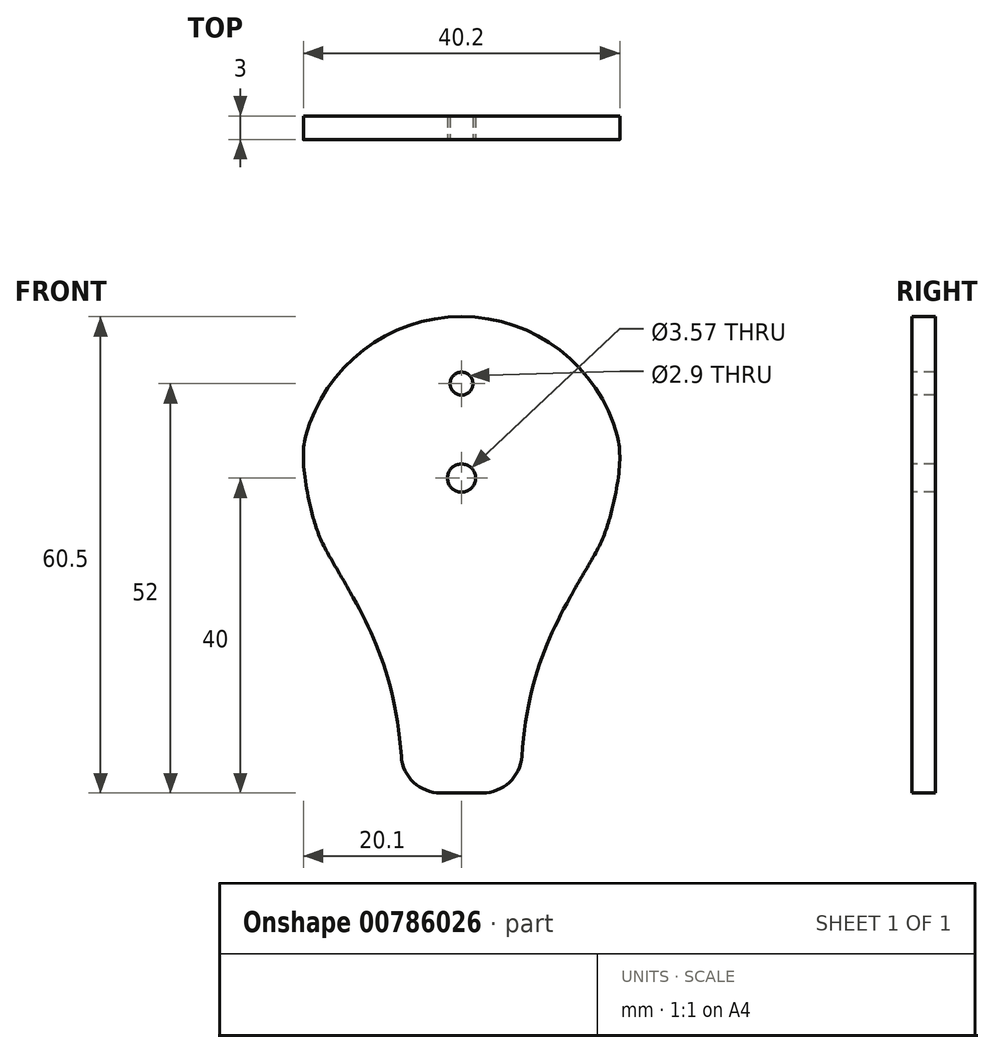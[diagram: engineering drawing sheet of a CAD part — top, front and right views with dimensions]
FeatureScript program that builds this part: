
annotation { "Feature Type Name" : "Feature", "Feature Type Description" : "" }
export const myFeature = defineFeature(function(context is Context, id is Id, definition is map)
    precondition{}
    {
        {
            var Q0;
            Q0=qCreatedBy(makeId("Front.planeOp"),FACE);
            var sketch = newSketch(context, id + "F0", { "sketchPlane" : qUnion([Q0])});
            skLineSegment(sketch, "E0.bottom", {"start": v(7.5, 0) * mm, "end": v(-7.5, 0) * mm, "construction": true});
            skLineSegment(sketch, "E0.top", {"start": v(7.5, -40) * mm, "end": v(-7.5, -40) * mm});
            skLineSegment(sketch, "E0.left", {"start": v(7.5, 0) * mm, "end": v(7.5, -40) * mm, "construction": true});
            skLineSegment(sketch, "E0.right", {"start": v(-7.5, 0) * mm, "end": v(-7.5, -40) * mm, "construction": true});
            skPoint(sketch, "E0.middle", {"position": v(0, -20) * mm});
            skCircle(sketch, "E1", {"center": v(0, 0) * mm, "radius": 19.5 * mm});
            skCircle(sketch, "E2", {"center": v(0, 0) * mm, "radius": 20.5 * mm});
            skLineSegment(sketch, "E3", {"start": v(0, 0) * mm, "end": v(19.8, 5.3) * mm, "construction": true});
            skLineSegment(sketch, "E4", {"start": v(0, 0) * mm, "end": v(18.84, -5.05) * mm, "construction": true});
            skLineSegment(sketch, "E5", {"start": v(0, 0) * mm, "end": v(16.89, -9.75) * mm, "construction": true});
            skLineSegment(sketch, "E6", {"start": v(0, 0) * mm, "end": v(17.75, 10.25) * mm, "construction": true});
            skLineSegment(sketch, "E7", {"start": v(19.8, 5.3) * mm, "end": v(19.8, 5.3) * mm});
            skLineSegment(sketch, "E8", {"start": v(16.89, -9.75) * mm, "end": v(11.89, -18.41) * mm});
            skLineSegment(sketch, "E9", {"start": v(0, -40) * mm, "end": v(0, 20.5) * mm, "construction": true});
            skFitSpline(sketch, "E10.MirrorCS", {"points": [v(-16.89, -9.75) * mm, v(-7.5, -40) * mm], "startDerivative": vector(15, -25.98) * mm, "endDerivative": vector(0, -45) * mm});
            skLineSegment(sketch, "E11.MirrorCS", {"start": v(0, 0) * mm, "end": v(-17.75, 10.25) * mm});
            skFitSpline(sketch, "E12", {"points": [v(19.8, 5.3) * mm, v(18.84, -5.05) * mm], "startDerivative": vector(1.96, -7.3) * mm, "endDerivative": vector(-3.42, -12.77) * mm});
            skLineSegment(sketch, "E13", {"start": v(19.8, 5.3) * mm, "end": v(20.45, 2.87) * mm, "construction": true});
            skLineSegment(sketch, "E14", {"start": v(18.84, -5.05) * mm, "end": v(19.98, -0.79) * mm, "construction": true});
            skLineSegment(sketch, "E15.MirrorCS", {"start": v(0, 0) * mm, "end": v(-17.75, 10.25) * mm, "construction": true});
            skLineSegment(sketch, "E16.MirrorCS", {"start": v(0, 0) * mm, "end": v(-19.8, 5.3) * mm, "construction": true});
            skLineSegment(sketch, "E17.MirrorCS", {"start": v(0, 0) * mm, "end": v(-18.84, -5.05) * mm, "construction": true});
            skLineSegment(sketch, "E18.MirrorCS", {"start": v(0, 0) * mm, "end": v(-16.89, -9.75) * mm, "construction": true});
            skFitSpline(sketch, "E19.MirrorCS", {"points": [v(-19.8, 5.3) * mm, v(-18.84, -5.05) * mm], "startDerivative": vector(-1.96, -7.3) * mm, "endDerivative": vector(3.42, -12.77) * mm});
            skFitSpline(sketch, "E20.MirrorCS", {"points": [v(16.89, -9.75) * mm, v(7.5, -40) * mm], "startDerivative": vector(-15, -25.98) * mm, "endDerivative": vector(0, -45) * mm});
            skLineSegment(sketch, "E21.bottom", {"start": v(-7.5, -40) * mm, "end": v(7.5, -40) * mm});
            skLineSegment(sketch, "E21.top", {"start": v(-7.5, -296) * mm, "end": v(7.5, -296) * mm});
            skLineSegment(sketch, "E21.left", {"start": v(-7.5, -40) * mm, "end": v(-7.5, -296) * mm});
            skLineSegment(sketch, "E21.right", {"start": v(7.5, -40) * mm, "end": v(7.5, -296) * mm});
            skLineSegment(sketch, "E22.bottom", {"start": v(2.87, -299) * mm, "end": v(-2.87, -299) * mm});
            skLineSegment(sketch, "E22.top", {"start": v(2.87, -293) * mm, "end": v(-2.87, -293) * mm});
            skLineSegment(sketch, "E22.left", {"start": v(2.87, -299) * mm, "end": v(2.87, -293) * mm});
            skLineSegment(sketch, "E22.right", {"start": v(-2.87, -299) * mm, "end": v(-2.87, -293) * mm});
            skPoint(sketch, "E22.middle", {"position": v(0, -296) * mm});
            skSolve(sketch);
        }
        {
            var Q0;
            {var subQ0=sQuery(id+"F0.wireOp",EDGE,"E19.MirrorCS");Q0=makeQuery(id+"F0.imprint","IMPRINT",FACE,{"disambiguationData":[TD([[makeQuery(id+"F0.imprint","IMPRINT",EDGE,{"derivedFrom":subQ0}),1.0]])]});}
            var Q1;
            {var subQ0=sQuery(id+"F0.wireOp",EDGE,"E12");Q1=makeQuery(id+"F0.imprint","IMPRINT",FACE,{"disambiguationData":[TD([[makeQuery(id+"F0.imprint","IMPRINT",EDGE,{"derivedFrom":subQ0}),-1.0]])]});}
            var Q2;
            {var subQ0=sQuery(id+"F0.wireOp",EDGE,"E1");var subQ4=makeQuery(id+"F0.imprint","INTERSECT",VERTEX,{"derivedFrom":[subQ0,sQuery(id+"F0.wireOp",EDGE,"E19.MirrorCS")]});Q2=makeQuery(id+"F0.imprint","IMPRINT",FACE,{"disambiguationData":[TD([[makeQuery(id+"F0.imprint","IMPRINT",EDGE,{"disambiguationData":[TD([[subQ4,1.0]])],"derivedFrom":subQ0}),1.0]])]});}
            var Q3;
            {var subQ3=sQuery(id+"F0.wireOp",EDGE,"E10.MirrorCS");var subQ5=sQuery(id+"F0.wireOp",EDGE,"E2");var subQ6=makeQuery(id+"F0.imprint","INTERSECT",VERTEX,{"derivedFrom":[subQ5,subQ3]});Q3=makeQuery(id+"F0.imprint","IMPRINT",FACE,{"disambiguationData":[TD([[makeQuery(id+"F0.imprint","IMPRINT",EDGE,{"disambiguationData":[TD([[subQ6,-1.0]])],"derivedFrom":subQ5}),1.0]])]});}
            var Q4;
            {var subQ1=sQuery(id+"F0.wireOp",EDGE,"E0.top");Q4=makeQuery(id+"F0.imprint","IMPRINT",FACE,{"disambiguationData":[TD([[makeQuery(id+"F0.imprint","IMPRINT",EDGE,{"derivedFrom":subQ1}),-1.0]])]});}
            var Q5;
            {var subQ0=sQuery(id+"F0.wireOp",EDGE,"E8");var subQ1=sQuery(id+"F0.wireOp",EDGE,"E2");var subQ2=makeQuery(id+"F0.imprint","INTERSECT",VERTEX,{"derivedFrom":[subQ1,subQ0]});Q5=makeQuery(id+"F0.imprint","IMPRINT",FACE,{"disambiguationData":[TD([[makeQuery(id+"F0.imprint","IMPRINT",EDGE,{"disambiguationData":[TD([[subQ2,-1.0]])],"derivedFrom":subQ1}),1.0]])]});}
            var Q6;
            {var subQ0=sQuery(id+"F0.wireOp",EDGE,"E21.bottom");Q6=makeQuery(id+"F0.imprint","IMPRINT",FACE,{"disambiguationData":[TD([[makeQuery(id+"F0.imprint","IMPRINT",EDGE,{"derivedFrom":subQ0}),1.0]])]});}
            var Q7;
            Q7=makeQuery(id+"F0.imprint","IMPRINT",FACE,{"disambiguationData":[TD([[makeQuery(id+"F0.imprint","IMPRINT",EDGE,{"derivedFrom":sQuery(id+"F0.wireOp",EDGE,"E21.bottom")}),-1.0]])]});
            extrude(context, id + "F1", {"entities" : qUnion([Q0, Q1, Q2, Q3, Q4, Q5, Q6, Q7]), "depth" : 3 * mm, "offsetDistance" : 25 * mm});
        }
        {
            var Q0;
            Q0=makeQuery(id+"F1.opExtrude","CAP_FACE",FACE,{"disambiguationData":[OSD([sQuery(id+"F0.wireOp",EDGE,"E0.top"),sQuery(id+"F0.wireOp",EDGE,"E1"),sQuery(id+"F0.wireOp",EDGE,"E2"),sQuery(id+"F0.wireOp",EDGE,"7a9026b3-197f-48e2-9b81-13cee80a4807"),sQuery(id+"F0.wireOp",EDGE,"0a668d27-42bc-4e6d-9f5e-2706f69a0711"),sQuery(id+"F0.wireOp",EDGE,"f3387c69-d86e-4529-9347-0b486354b344.MirrorCS"),sQuery(id+"F0.wireOp",EDGE,"E10.MirrorCS")])],"isStart":false});
            var sketch = newSketch(context, id + "F2", { "sketchPlane" : qUnion([Q0])});
            skCircle(sketch, "E23", {"center": v(0, 0) * mm, "radius": 1.79 * mm});
            skSolve(sketch);
        }
        {
            var Q0;
            Q0=qSketchRegion(id+"F2",true);
            extrude(context, id + "F3", {"entities" : qUnion([Q0]), "operationType" : NewBodyOperationType.REMOVE, "oppositeDirection" : true, "depth" : 25 * mm, "offsetDistance" : 25 * mm});
        }
        {
            var Q0;
            Q0=makeQuery(id+"F1.opExtrude","SWEPT_EDGE",EDGE,{"disambiguationData":[OSD([sQuery(id+"F0.wireOp",EDGE,"E21.top"),sQuery(id+"F0.wireOp",EDGE,"E21.left")])]});
            var Q1;
            Q1=makeQuery(id+"F1.opExtrude","SWEPT_EDGE",EDGE,{"disambiguationData":[OSD([sQuery(id+"F0.wireOp",EDGE,"E21.top"),sQuery(id+"F0.wireOp",EDGE,"E21.right")])]});
            fillet(context, id + "F4", {"entities" : qUnion([Q0, Q1]), "radius" : 5 * mm, "tangentPropagation" : true, "allowEdgeOverflow" : false});
        }
        {
            var Q0;
            Q0=makeQuery(id+"F1.opExtrude","CAP_FACE",FACE,{"disambiguationData":[OSD([sQuery(id+"F0.wireOp",EDGE,"E1"),sQuery(id+"F0.wireOp",EDGE,"E2"),sQuery(id+"F0.wireOp",EDGE,"E10.MirrorCS"),sQuery(id+"F0.wireOp",EDGE,"E12"),sQuery(id+"F0.wireOp",EDGE,"E19.MirrorCS"),sQuery(id+"F0.wireOp",EDGE,"E20.MirrorCS"),sQuery(id+"F0.wireOp",EDGE,"E21.top"),sQuery(id+"F0.wireOp",EDGE,"E21.left"),sQuery(id+"F0.wireOp",EDGE,"E21.right"),sQuery(id+"F0.wireOp",EDGE,"E22.top"),sQuery(id+"F0.wireOp",EDGE,"E22.left"),sQuery(id+"F0.wireOp",EDGE,"E22.right")])],"isStart":false});
            var sketch = newSketch(context, id + "F5", { "sketchPlane" : qUnion([Q0])});
            skCircle(sketch, "E24", {"center": v(2.87, -293) * mm, "radius": 0.5 * mm});
            skCircle(sketch, "E25", {"center": v(-2.87, -293) * mm, "radius": 0.5 * mm});
            skSolve(sketch);
        }
        {
            var Q0;
            {var subQ4=sQuery(id+"F0.wireOp",EDGE,"E2");Q0=makeQuery(id+"F5.imprint","IMPRINT",FACE,{"disambiguationData":[TD([[makeQuery(id+"F5.imprint","IMPRINT",EDGE,{"derivedFrom":makeQuery(id+"F1.opExtrude","CAP_EDGE",EDGE,{"disambiguationData":[OSD([subQ4])],"isStart":false})}),1.0]])]});}
            var sketch = newSketch(context, id + "F6", { "sketchPlane" : qUnion([Q0])});
            skCircle(sketch, "E26", {"center": v(0, 12) * mm, "radius": 1.45 * mm});
            skSolve(sketch);
        }
        {
            var Q0;
            Q0=qSketchRegion(id+"F6",true);
            extrude(context, id + "F7", {"entities" : qUnion([Q0]), "operationType" : NewBodyOperationType.REMOVE, "oppositeDirection" : true, "depth" : 25 * mm, "offsetDistance" : 25 * mm});
        }
        {
            var Q0;
            {var subQ4=sQuery(id+"F0.wireOp",EDGE,"E2");Q0=makeQuery(id+"F5.imprint","IMPRINT",FACE,{"disambiguationData":[TD([[makeQuery(id+"F5.imprint","IMPRINT",EDGE,{"derivedFrom":makeQuery(id+"F1.opExtrude","CAP_EDGE",EDGE,{"disambiguationData":[OSD([subQ4])],"isStart":false})}),1.0]])]});}
            var sketch = newSketch(context, id + "F8", { "sketchPlane" : qUnion([Q0])});
            skCircle(sketch, "E27", {"center": v(0, -200) * mm, "radius": 1.45 * mm});
            skCircle(sketch, "E28.0.1.0", {"center": v(0, -210) * mm, "radius": 1.45 * mm});
            skCircle(sketch, "E28.0.2.0", {"center": v(0, -220) * mm, "radius": 1.45 * mm});
            skCircle(sketch, "E28.0.3.0", {"center": v(0, -230) * mm, "radius": 1.45 * mm});
            skCircle(sketch, "E28.0.4.0", {"center": v(0, -240) * mm, "radius": 1.45 * mm});
            skCircle(sketch, "E28.0.5.0", {"center": v(0, -250) * mm, "radius": 1.45 * mm});
            skCircle(sketch, "E28.0.6.0", {"center": v(0, -260) * mm, "radius": 1.45 * mm});
            skCircle(sketch, "E28.0.7.0", {"center": v(0, -270) * mm, "radius": 1.45 * mm});
            skCircle(sketch, "E28.0.8.0", {"center": v(0, -280) * mm, "radius": 1.45 * mm});
            skLineSegment(sketch, "E28.direction1", {"start": v(0, -200) * mm, "end": v(35.2, -200) * mm, "construction": true});
            skLineSegment(sketch, "E28.direction2", {"start": v(0, -200) * mm, "end": v(0, -210) * mm, "construction": true});
            skSolve(sketch);
        }
        {
            var Q0;
            Q0=qSketchRegion(id+"F8",true);
            extrude(context, id + "F9", {"entities" : qUnion([Q0]), "operationType" : NewBodyOperationType.REMOVE, "oppositeDirection" : true, "depth" : 25 * mm, "offsetDistance" : 25 * mm});
        }
    });
